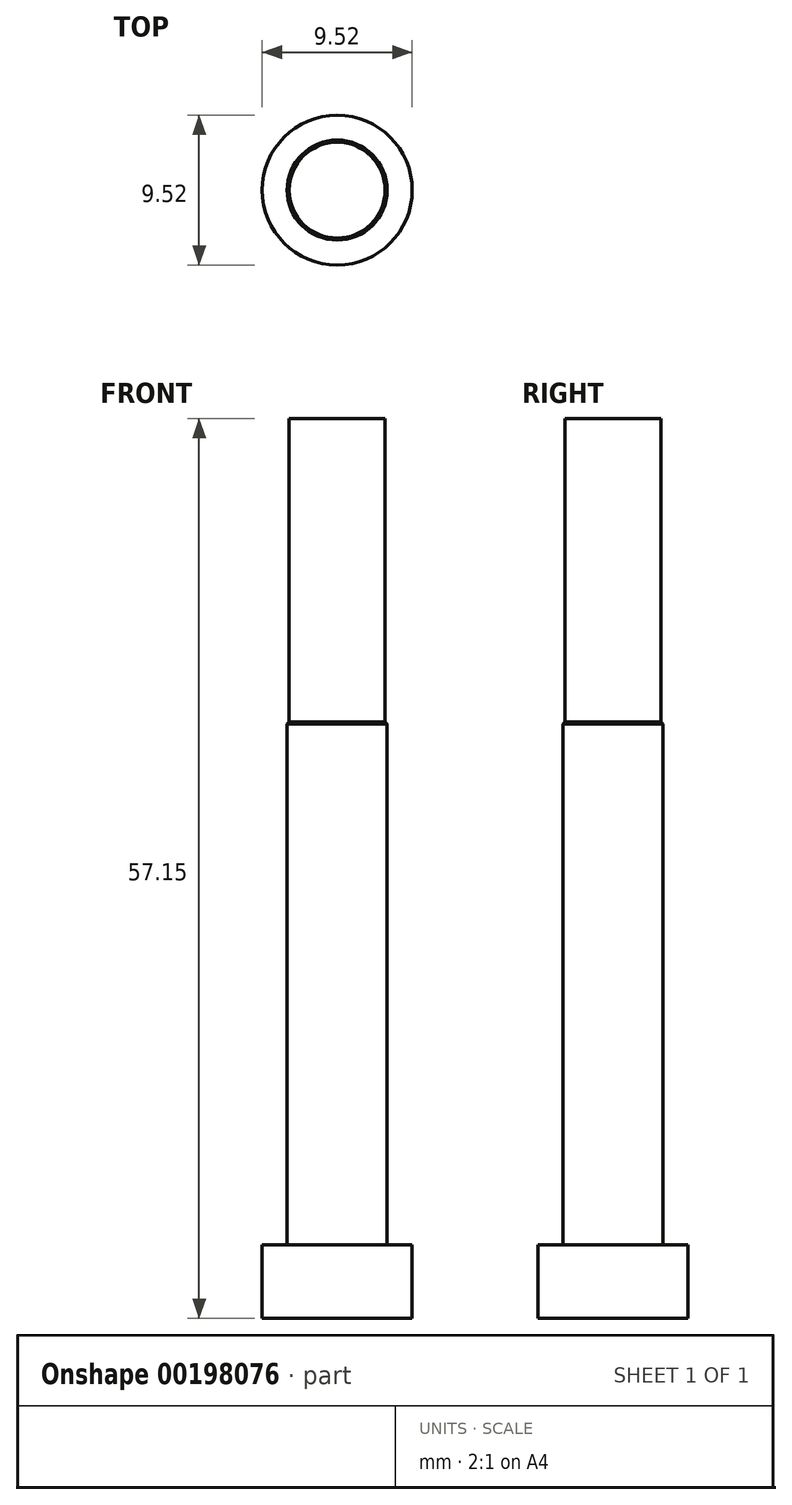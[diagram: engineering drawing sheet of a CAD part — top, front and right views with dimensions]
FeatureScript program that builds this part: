
annotation { "Feature Type Name" : "Feature", "Feature Type Description" : "" }
export const myFeature = defineFeature(function(context is Context, id is Id, definition is map)
    precondition{}
    {
        {
            var Q0;
            Q0=qCreatedBy(makeId("Right.planeOp"),FACE);
            var sketch = newSketch(context, id + "F0", { "sketchPlane" : qUnion([Q0])});
            skLineSegment(sketch, "E0", {"start": v(0, 0) * mm, "end": v(4.76, 0) * mm});
            skLineSegment(sketch, "E1", {"start": v(4.76, 0) * mm, "end": v(4.76, 4.67) * mm});
            skLineSegment(sketch, "E2", {"start": v(4.76, 4.67) * mm, "end": v(3.18, 4.67) * mm});
            skLineSegment(sketch, "E3", {"start": v(3.18, 4.67) * mm, "end": v(3.18, 38) * mm});
            skLineSegment(sketch, "E4", {"start": v(3.05, 38) * mm, "end": v(3.05, 57.15) * mm});
            skLineSegment(sketch, "E5", {"start": v(3.05, 38) * mm, "end": v(3.18, 38) * mm});
            skLineSegment(sketch, "E6", {"start": v(3.05, 57.15) * mm, "end": v(0, 57.15) * mm});
            skLineSegment(sketch, "E7", {"start": v(0, 57.15) * mm, "end": v(0, 0) * mm});
            skSolve(sketch);
        }
        {
            var Q0;
            Q0=makeQuery(id+"F0.imprint","IMPRINT",FACE,{"disambiguationData":[TD([[makeQuery(id+"F0.imprint","IMPRINT",EDGE,{"derivedFrom":sQuery(id+"F0.wireOp",EDGE,"E0")}),1.0]])]});
            var Q1;
            Q1=sQuery(id+"F0.wireOp",EDGE,"E7");
            revolve(context, id + "F1", {"entities" : qUnion([Q0]), "axis" : qUnion([Q1]), "revolveType" : RevolveType.FULL});
        }
        {
            var Q0;
            Q0=makeQuery(id+"F1.opRevolve","SWEPT_EDGE",EDGE,{"disambiguationData":[OSD([sQuery(id+"F0.wireOp",EDGE,"E3"),sQuery(id+"F0.wireOp",EDGE,"E5")])]});
            chamfer(context, id + "F2", {"entities" : qUnion([Q0]), "width" : 0.25 * mm, "tangentPropagation" : true});
        }
    });
